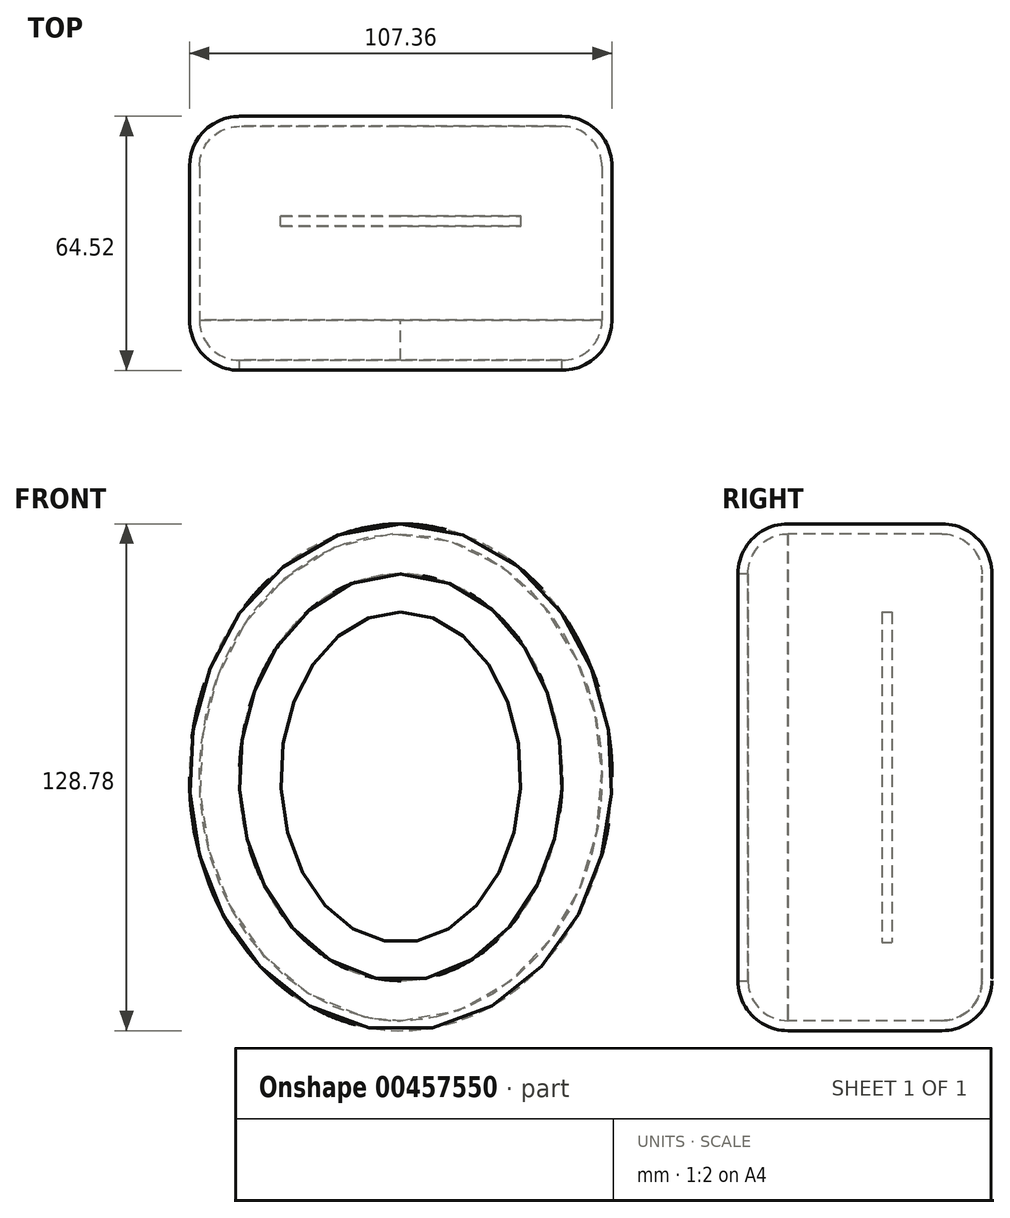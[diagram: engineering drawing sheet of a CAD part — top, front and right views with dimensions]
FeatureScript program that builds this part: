
annotation { "Feature Type Name" : "Feature", "Feature Type Description" : "" }
export const myFeature = defineFeature(function(context is Context, id is Id, definition is map)
    precondition{}
    {
        {
            var Q0;
            Q0=qCreatedBy(makeId("Front.planeOp"),FACE);
            var sketch = newSketch(context, id + "F0", { "sketchPlane" : qUnion([Q0])});
            skEllipse(sketch, "E0", {"center": v(0, 0) * mm, "majorRadius": 64.39 * mm, "minorRadius": 53.68 * mm, "majorAxis": v(0, 1)});
            skSolve(sketch);
        }
        {
            var Q0;
            Q0=qSketchRegion(id+"F0",true);
            extrude(context, id + "F1", {"entities" : qUnion([Q0]), "depth" : 39.12 * mm, "hasSecondDirection" : true, "secondDirectionOppositeDirection" : true, "secondDirectionDepth" : 25.4 * mm});
        }
        {
            var Q0;
            Q0=makeQuery(id+"F1.opExtrude","CAP_EDGE",EDGE,{"disambiguationData":[OSD([sQuery(id+"F0.wireOp",EDGE,"E0")])],"isStart":false});
            var Q1;
            Q1=makeQuery(id+"F1.opExtrude","CAP_EDGE",EDGE,{"disambiguationData":[OSD([sQuery(id+"F0.wireOp",EDGE,"E0")])],"isStart":true});
            fillet(context, id + "F2", {"entities" : qUnion([Q0, Q1]), "radius" : 12.7 * mm, "tangentPropagation" : true, "allowEdgeOverflow" : false});
        }
        {
            var Q0;
            Q0=makeQuery(id+"F1.opExtrude","CAP_FACE",FACE,{"disambiguationData":[OSD([sQuery(id+"F0.wireOp",EDGE,"E0")])],"isStart":false});
            shell(context, id + "F3", {"entities" : qUnion([Q0]), "thickness" : 2.54 * mm});
        }
        {
            var Q0;
            Q0=qCreatedBy(makeId("Front.planeOp"),FACE);
            var sketch = newSketch(context, id + "F4", { "sketchPlane" : qUnion([Q0])});
            skLineSegment(sketch, "E1.bottom", {"start": v(-17.39, 27.2) * mm, "end": v(17.39, 27.2) * mm});
            skLineSegment(sketch, "E1.top", {"start": v(-17.39, -27.2) * mm, "end": v(17.39, -27.2) * mm});
            skLineSegment(sketch, "E1.left", {"start": v(-17.39, 27.2) * mm, "end": v(-17.39, -27.2) * mm});
            skLineSegment(sketch, "E1.right", {"start": v(17.39, 27.2) * mm, "end": v(17.39, -27.2) * mm});
            skPoint(sketch, "E1.middle", {"position": v(0, 0) * mm});
            skSolve(sketch);
        }
        {
            var Q0;
            Q0 = qSketchRegion(id + "F4", true);
            extrude(context, id + "F5", {"entities" : qUnion([Q0]), "depth" : 2.54 * mm});
        }
        {
            var Q0;
            Q0=qCreatedBy(makeId("Front.planeOp"),FACE);
            var sketch = newSketch(context, id + "F6", { "sketchPlane" : qUnion([Q0])});
            skEllipse(sketch, "E2", {"center": v(0, 0) * mm, "majorRadius": 41.99 * mm, "minorRadius": 30.54 * mm, "majorAxis": v(0, 1)});
            skSolve(sketch);
        }
        {
            var Q0;
            Q0 = qSketchRegion(id + "F6", true);
            extrude(context, id + "F7", {"entities" : qUnion([Q0]), "operationType" : NewBodyOperationType.ADD, "depth" : 2.54 * mm});
        }
        {
            var Q0;
            Q0=makeQuery(id+"F7.boolean.opBoolean","MERGE",FACE,{"derivedFrom":[makeQuery(id+"F5.opExtrude","CAP_FACE",FACE,{"disambiguationData":[OSD([sQuery(id+"F4.wireOp",EDGE,"E1.bottom"),sQuery(id+"F4.wireOp",EDGE,"E1.top"),sQuery(id+"F4.wireOp",EDGE,"E1.left"),sQuery(id+"F4.wireOp",EDGE,"E1.right")])],"isStart":false}),makeQuery(id+"F7.opExtrude","CAP_FACE",FACE,{"disambiguationData":[OSD([sQuery(id+"F6.wireOp",EDGE,"E2")])],"isStart":false})]});
            shell(context, id + "F8", {"entities" : qUnion([Q0]), "thickness" : 2.54 * mm});
        }
    });
